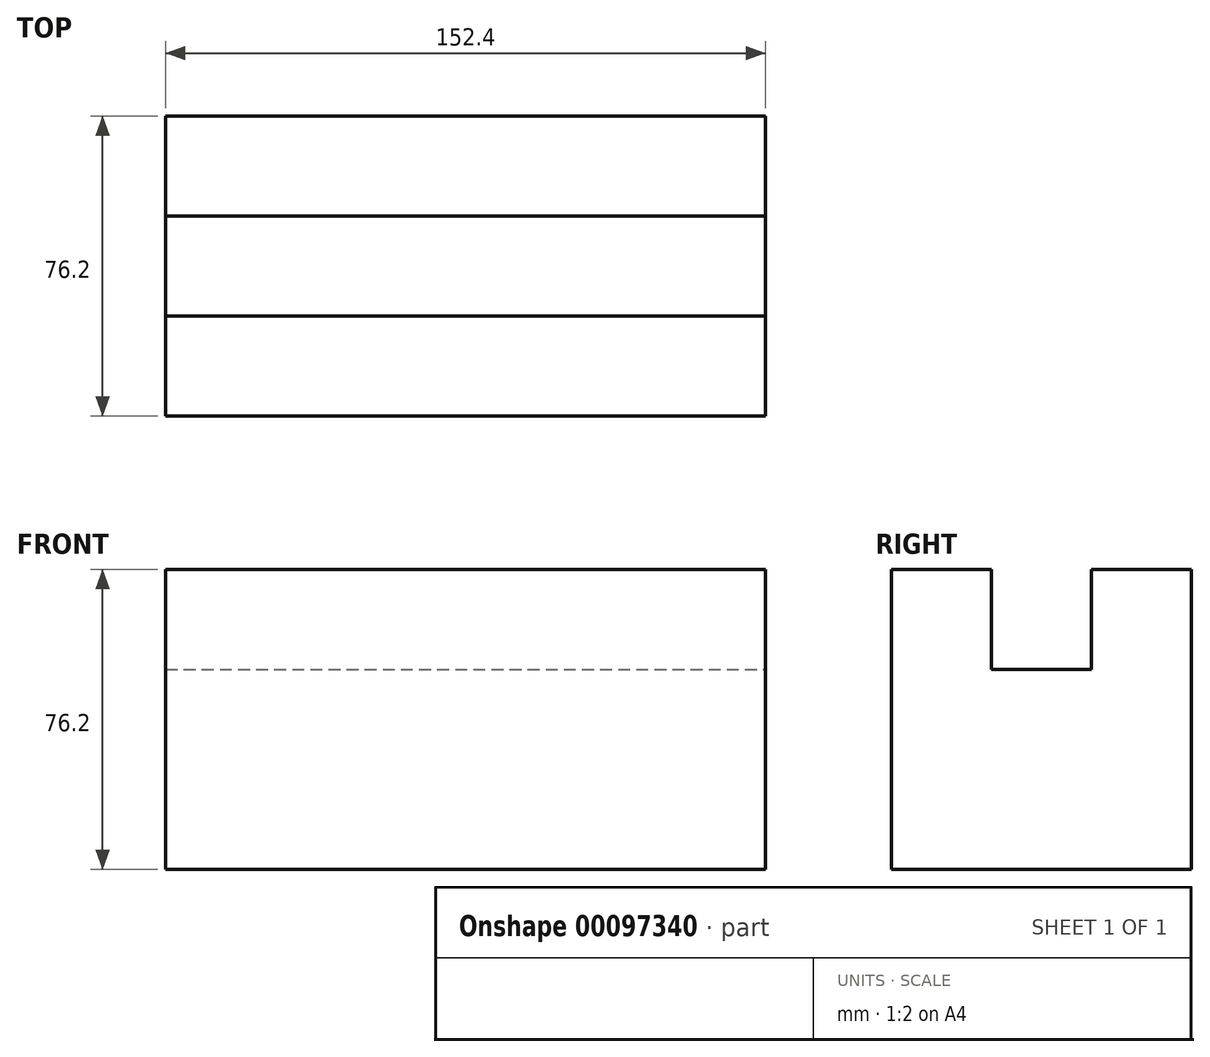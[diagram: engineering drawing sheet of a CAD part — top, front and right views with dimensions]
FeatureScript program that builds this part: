
annotation { "Feature Type Name" : "Feature", "Feature Type Description" : "" }
export const myFeature = defineFeature(function(context is Context, id is Id, definition is map)
    precondition{}
    {
        {
            var Q0;
            Q0=qCreatedBy(makeId("Front.planeOp"),FACE);
            var sketch = newSketch(context, id + "F0", { "sketchPlane" : qUnion([Q0])});
            skLineSegment(sketch, "E0.bottom", {"start": v(-76.2, 0) * mm, "end": v(76.2, 0) * mm});
            skLineSegment(sketch, "E0.top", {"start": v(-76.2, 76.2) * mm, "end": v(76.2, 76.2) * mm});
            skLineSegment(sketch, "E0.left", {"start": v(-76.2, 0) * mm, "end": v(-76.2, 76.2) * mm});
            skLineSegment(sketch, "E0.right", {"start": v(76.2, 0) * mm, "end": v(76.2, 76.2) * mm});
            skSolve(sketch);
        }
        {
            var Q0;
            Q0=makeQuery(id+"F0.imprint","IMPRINT",FACE,{"disambiguationData":[TD([[makeQuery(id+"F0.imprint","IMPRINT",EDGE,{"derivedFrom":sQuery(id+"F0.wireOp",EDGE,"E0.bottom")}),1.0]])]});
            extrude(context, id + "F1", {"entities" : qUnion([Q0]), "depth" : 76.2 * mm, "symmetric" : true});
        }
        {
            var Q0;
            Q0=makeQuery(id+"F1.opExtrude","SWEPT_FACE",FACE,{"disambiguationData":[OSD([sQuery(id+"F0.wireOp",EDGE,"E0.right")])]});
            var sketch = newSketch(context, id + "F2", { "sketchPlane" : qUnion([Q0])});
            skLineSegment(sketch, "E1.bottom", {"start": v(-12.7, 76.2) * mm, "end": v(12.7, 76.2) * mm});
            skLineSegment(sketch, "E1.top", {"start": v(-12.7, 50.8) * mm, "end": v(12.7, 50.8) * mm});
            skLineSegment(sketch, "E1.left", {"start": v(-12.7, 76.2) * mm, "end": v(-12.7, 50.8) * mm});
            skLineSegment(sketch, "E1.right", {"start": v(12.7, 76.2) * mm, "end": v(12.7, 50.8) * mm});
            skSolve(sketch);
        }
        {
            var Q0;
            Q0=makeQuery(id+"F2.imprint","IMPRINT",FACE,{"disambiguationData":[TD([[makeQuery(id+"F2.imprint","IMPRINT",EDGE,{"derivedFrom":sQuery(id+"F2.wireOp",EDGE,"E1.bottom")}),-1.0]])]});
            extrude(context, id + "F3", {"entities" : qUnion([Q0]), "operationType" : NewBodyOperationType.REMOVE, "endBound" : BoundingType.THROUGH_ALL, "oppositeDirection" : true, "depth" : 25.4 * mm});
        }
    });
